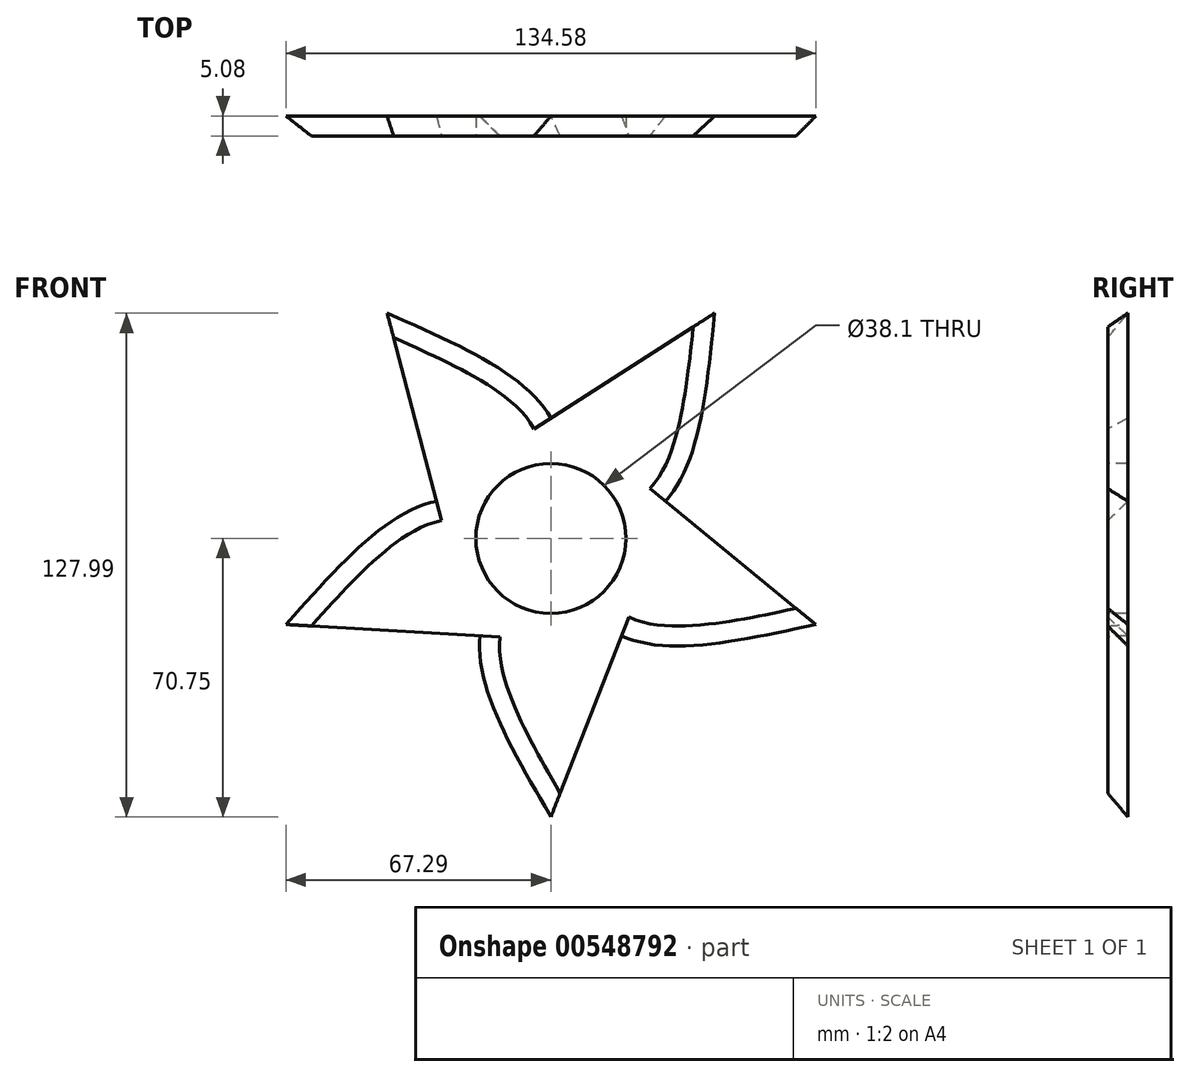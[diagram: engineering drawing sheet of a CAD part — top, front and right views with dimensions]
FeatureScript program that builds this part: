
annotation { "Feature Type Name" : "Feature", "Feature Type Description" : "" }
export const myFeature = defineFeature(function(context is Context, id is Id, definition is map)
    precondition{}
    {
        {
            var Q0;
            Q0=qCreatedBy(makeId("Front.planeOp"),FACE);
            var sketch = newSketch(context, id + "F0", { "sketchPlane" : qUnion([Q0])});
            skLineSegment(sketch, "E0.0", {"start": v(-41.59, 57.24) * mm, "end": v(41.59, 57.24) * mm});
            skLineSegment(sketch, "E0.1", {"start": v(41.59, 57.24) * mm, "end": v(67.3, -21.86) * mm});
            skLineSegment(sketch, "E0.2", {"start": v(67.3, -21.86) * mm, "end": v(0, -70.75) * mm});
            skLineSegment(sketch, "E0.3", {"start": v(0, -70.75) * mm, "end": v(-67.3, -21.86) * mm});
            skLineSegment(sketch, "E0.4", {"start": v(-67.3, -21.86) * mm, "end": v(-41.59, 57.24) * mm});
            skPoint(sketch, "E0.0.midPoint", {"position": v(0, 57.24) * mm});
            skLineSegment(sketch, "E1", {"start": v(-67.3, -21.86) * mm, "end": v(0, 0) * mm});
            skLineSegment(sketch, "E2", {"start": v(-41.59, 57.24) * mm, "end": v(0, 0) * mm});
            skLineSegment(sketch, "E3", {"start": v(41.59, 57.24) * mm, "end": v(0, 0) * mm});
            skLineSegment(sketch, "E4", {"start": v(0, -70.75) * mm, "end": v(0, 0) * mm});
            skLineSegment(sketch, "E5", {"start": v(67.3, -21.86) * mm, "end": v(0, 0) * mm});
            skPoint(sketch, "E6.0.midPoint", {"position": v(0, -24.72) * mm});
            skPoint(sketch, "E7", {"position": v(0, 30.56) * mm});
            skPoint(sketch, "E8", {"position": v(-29.07, 9.44) * mm});
            skPoint(sketch, "E9", {"position": v(-17.96, -24.72) * mm});
            skPoint(sketch, "E10", {"position": v(17.96, -24.72) * mm});
            skPoint(sketch, "E11", {"position": v(29.07, 9.44) * mm});
            skFitSpline(sketch, "E12", {"points": [v(-67.3, -21.86) * mm, v(-29.07, 9.44) * mm, v(0, 0) * mm], "startDerivative": vector(68.92, 77.59) * mm, "endDerivative": vector(65.52, -38.49) * mm});
            skFitSpline(sketch, "E13", {"points": [v(-41.59, 57.24) * mm, v(0, 30.56) * mm, v(0, 0) * mm], "startDerivative": vector(95.09, -41.57) * mm, "endDerivative": vector(-16.35, -74.2) * mm});
            skFitSpline(sketch, "E14", {"points": [v(41.59, 57.24) * mm, v(29.07, 9.44) * mm, v(0, 0) * mm], "startDerivative": vector(-10.15, -103.28) * mm, "endDerivative": vector(-75.63, -7.38) * mm});
            skFitSpline(sketch, "E15", {"points": [v(67.3, -21.86) * mm, v(17.96, -24.72) * mm, v(0, 0) * mm], "startDerivative": vector(-101.37, -22.26) * mm, "endDerivative": vector(-30.39, 69.65) * mm});
            skFitSpline(sketch, "E16", {"points": [v(0, -70.75) * mm, v(-17.96, -24.72) * mm, v(0, 0) * mm], "startDerivative": vector(-52.5, 89.53) * mm, "endDerivative": vector(56.85, 50.42) * mm});
            skPoint(sketch, "E17", {"position": v(2.74, 20) * mm});
            skPoint(sketch, "E18", {"position": v(19.87, 3.58) * mm});
            skPoint(sketch, "E19", {"position": v(9.54, -17.8) * mm});
            skPoint(sketch, "E20", {"position": v(-13.97, -14.57) * mm});
            skPoint(sketch, "E21", {"position": v(-18.18, 8.78) * mm});
            skLineSegment(sketch, "E22", {"start": v(9.54, -17.8) * mm, "end": v(0, -70.75) * mm});
            skLineSegment(sketch, "E23", {"start": v(19.87, 3.58) * mm, "end": v(67.3, -21.86) * mm});
            skLineSegment(sketch, "E24", {"start": v(-13.97, -14.57) * mm, "end": v(-67.3, -21.86) * mm});
            skLineSegment(sketch, "E25", {"start": v(-29.07, 9.44) * mm, "end": v(-41.59, 57.24) * mm});
            skLineSegment(sketch, "E26", {"start": v(0, 30.56) * mm, "end": v(41.59, 57.24) * mm});
            skLineSegment(sketch, "E27", {"start": v(29.07, 9.44) * mm, "end": v(67.3, -21.86) * mm});
            skLineSegment(sketch, "E28", {"start": v(17.96, -24.72) * mm, "end": v(0, -70.75) * mm});
            skLineSegment(sketch, "E29", {"start": v(-67.3, -21.86) * mm, "end": v(-17.96, -24.72) * mm});
            skLineSegment(sketch, "E30", {"start": v(-41.59, 57.24) * mm, "end": v(-18.18, 8.78) * mm});
            skLineSegment(sketch, "E31", {"start": v(2.74, 20) * mm, "end": v(41.59, 57.24) * mm});
            skLineSegment(sketch, "E32", {"start": v(-41.59, 57.24) * mm, "end": v(-34.1, 41.72) * mm});
            skLineSegment(sketch, "E33", {"start": v(-34.1, 41.72) * mm, "end": v(-22.08, 16.87) * mm});
            skLineSegment(sketch, "E34", {"start": v(9.23, 26.22) * mm, "end": v(29.16, 45.32) * mm});
            skLineSegment(sketch, "E35", {"start": v(27.8, -0.67) * mm, "end": v(52.12, -13.72) * mm});
            skLineSegment(sketch, "E36", {"start": v(3.05, -53.8) * mm, "end": v(7.95, -26.64) * mm});
            skLineSegment(sketch, "E37", {"start": v(-50.23, -19.53) * mm, "end": v(-22.88, -15.8) * mm});
            skSolve(sketch);
        }
        {
            var Q0;
            {var subQ0=sQuery(id+"F0.wireOp",EDGE,"E1");Q0=makeQuery(id+"F0.imprint","IMPRINT",FACE,{"disambiguationData":[TD([[makeQuery(id+"F0.imprint","IMPRINT",EDGE,{"derivedFrom":subQ0}),-1.0]])]});}
            var Q1;
            {var subQ0=sQuery(id+"F0.wireOp",EDGE,"E2");Q1=makeQuery(id+"F0.imprint","IMPRINT",FACE,{"disambiguationData":[TD([[makeQuery(id+"F0.imprint","IMPRINT",EDGE,{"derivedFrom":subQ0}),-1.0]])]});}
            var Q2;
            {var subQ0=sQuery(id+"F0.wireOp",EDGE,"E3");Q2=makeQuery(id+"F0.imprint","IMPRINT",FACE,{"disambiguationData":[TD([[makeQuery(id+"F0.imprint","IMPRINT",EDGE,{"derivedFrom":subQ0}),-1.0]])]});}
            var Q3;
            {var subQ0=sQuery(id+"F0.wireOp",EDGE,"E4");Q3=makeQuery(id+"F0.imprint","IMPRINT",FACE,{"disambiguationData":[TD([[makeQuery(id+"F0.imprint","IMPRINT",EDGE,{"derivedFrom":subQ0}),-1.0]])]});}
            var Q4;
            {var subQ0=sQuery(id+"F0.wireOp",EDGE,"E5");Q4=makeQuery(id+"F0.imprint","IMPRINT",FACE,{"disambiguationData":[TD([[makeQuery(id+"F0.imprint","IMPRINT",EDGE,{"derivedFrom":subQ0}),-1.0]])]});}
            var Q5;
            {var subQ0=sQuery(id+"F0.wireOp",EDGE,"E25");Q5=makeQuery(id+"F0.imprint","IMPRINT",FACE,{"disambiguationData":[TD([[makeQuery(id+"F0.imprint","IMPRINT",EDGE,{"derivedFrom":subQ0}),-1.0]])]});}
            var Q6;
            {var subQ0=sQuery(id+"F0.wireOp",EDGE,"E26");Q6=makeQuery(id+"F0.imprint","IMPRINT",FACE,{"disambiguationData":[TD([[makeQuery(id+"F0.imprint","IMPRINT",EDGE,{"derivedFrom":subQ0}),-1.0]])]});}
            var Q7;
            {var subQ0=sQuery(id+"F0.wireOp",EDGE,"E23");Q7=makeQuery(id+"F0.imprint","IMPRINT",FACE,{"disambiguationData":[TD([[makeQuery(id+"F0.imprint","IMPRINT",EDGE,{"derivedFrom":subQ0}),1.0]])]});}
            var Q8;
            {var subQ0=sQuery(id+"F0.wireOp",EDGE,"E22");Q8=makeQuery(id+"F0.imprint","IMPRINT",FACE,{"disambiguationData":[TD([[makeQuery(id+"F0.imprint","IMPRINT",EDGE,{"derivedFrom":subQ0}),1.0]])]});}
            var Q9;
            {var subQ0=sQuery(id+"F0.wireOp",EDGE,"E24");Q9=makeQuery(id+"F0.imprint","IMPRINT",FACE,{"disambiguationData":[TD([[makeQuery(id+"F0.imprint","IMPRINT",EDGE,{"derivedFrom":subQ0}),1.0]])]});}
            var Q10;
            {var subQ0=sQuery(id+"F0.wireOp",EDGE,"E1");Q10=makeQuery(id+"F0.imprint","IMPRINT",FACE,{"disambiguationData":[TD([[makeQuery(id+"F0.imprint","IMPRINT",EDGE,{"derivedFrom":subQ0}),1.0]])]});}
            var Q11;
            {var subQ0=sQuery(id+"F0.wireOp",EDGE,"E2");Q11=makeQuery(id+"F0.imprint","IMPRINT",FACE,{"disambiguationData":[TD([[makeQuery(id+"F0.imprint","IMPRINT",EDGE,{"derivedFrom":subQ0}),1.0]])]});}
            var Q12;
            {var subQ0=sQuery(id+"F0.wireOp",EDGE,"E3");Q12=makeQuery(id+"F0.imprint","IMPRINT",FACE,{"disambiguationData":[TD([[makeQuery(id+"F0.imprint","IMPRINT",EDGE,{"derivedFrom":subQ0}),1.0]])]});}
            var Q13;
            {var subQ0=sQuery(id+"F0.wireOp",EDGE,"E4");Q13=makeQuery(id+"F0.imprint","IMPRINT",FACE,{"disambiguationData":[TD([[makeQuery(id+"F0.imprint","IMPRINT",EDGE,{"derivedFrom":subQ0}),1.0]])]});}
            var Q14;
            {var subQ0=sQuery(id+"F0.wireOp",EDGE,"E5");Q14=makeQuery(id+"F0.imprint","IMPRINT",FACE,{"disambiguationData":[TD([[makeQuery(id+"F0.imprint","IMPRINT",EDGE,{"derivedFrom":subQ0}),1.0]])]});}
            extrude(context, id + "F1", {"entities" : qUnion([Q0, Q1, Q2, Q3, Q4, Q5, Q6, Q7, Q8, Q9, Q10, Q11, Q12, Q13, Q14]), "endBound" : BoundingType.SYMMETRIC, "depth" : 5.08 * mm, "offsetDistance" : 25.4 * mm});
        }
        {
            var Q0;
            Q0=makeQuery(id+"F1.opExtrude","CAP_EDGE",EDGE,{"disambiguationData":[OSD([sQuery(id+"F0.wireOp",EDGE,"E16")])],"isStart":false});
            var Q1;
            Q1=makeQuery(id+"F1.opExtrude","CAP_EDGE",EDGE,{"disambiguationData":[OSD([sQuery(id+"F0.wireOp",EDGE,"E15")])],"isStart":false});
            var Q2;
            Q2=makeQuery(id+"F1.opExtrude","CAP_EDGE",EDGE,{"disambiguationData":[OSD([sQuery(id+"F0.wireOp",EDGE,"E14")])],"isStart":false});
            var Q3;
            Q3=makeQuery(id+"F1.opExtrude","CAP_EDGE",EDGE,{"disambiguationData":[OSD([sQuery(id+"F0.wireOp",EDGE,"E13")])],"isStart":false});
            var Q4;
            Q4=makeQuery(id+"F1.opExtrude","CAP_EDGE",EDGE,{"disambiguationData":[OSD([sQuery(id+"F0.wireOp",EDGE,"E12")])],"isStart":false});
            chamfer(context, id + "F2", {"entities" : qUnion([Q0, Q1, Q2, Q3, Q4]), "width" : 5.08 * mm, "tangentPropagation" : true});
        }
        {
            var Q0;
            Q0=makeQuery(id+"F1.opExtrude","CAP_FACE",FACE,{"disambiguationData":[OSD([sQuery(id+"F0.wireOp",EDGE,"E12"),sQuery(id+"F0.wireOp",EDGE,"E13"),sQuery(id+"F0.wireOp",EDGE,"E14"),sQuery(id+"F0.wireOp",EDGE,"E15"),sQuery(id+"F0.wireOp",EDGE,"E16"),sQuery(id+"F0.wireOp",EDGE,"E25"),sQuery(id+"F0.wireOp",EDGE,"E26"),sQuery(id+"F0.wireOp",EDGE,"E27"),sQuery(id+"F0.wireOp",EDGE,"E28"),sQuery(id+"F0.wireOp",EDGE,"E29")])],"isStart":false});
            var sketch = newSketch(context, id + "F3", { "sketchPlane" : qUnion([Q0])});
            skCircle(sketch, "E38", {"center": v(0, 0) * mm, "radius": 19.05 * mm});
            skPoint(sketch, "E39", {"position": v(-34.06, 41.66) * mm});
            skPoint(sketch, "E40", {"position": v(-22.02, 16.8) * mm});
            skPoint(sketch, "E41", {"position": v(9.28, 26.24) * mm});
            skPoint(sketch, "E42", {"position": v(29.14, 45.28) * mm});
            skPoint(sketch, "E43", {"position": v(27.86, -0.77) * mm});
            skPoint(sketch, "E44", {"position": v(52.09, -13.78) * mm});
            skPoint(sketch, "E45", {"position": v(7.96, -26.69) * mm});
            skPoint(sketch, "E46", {"position": v(3.1, -53.8) * mm});
            skPoint(sketch, "E47", {"position": v(-22.85, -15.81) * mm});
            skPoint(sketch, "E48", {"position": v(-50.2, -19.54) * mm});
            skCircle(sketch, "E49", {"center": v(0, 0) * mm, "radius": 27.83 * mm});
            skPoint(sketch, "E50", {"position": v(-10.99, 25.57) * mm});
            skPoint(sketch, "E51", {"position": v(-4.29, 27.8) * mm});
            skPoint(sketch, "E52", {"position": v(25.12, 12.67) * mm});
            skPoint(sketch, "E53", {"position": v(20.9, 18.38) * mm});
            skPoint(sketch, "E54", {"position": v(19.82, -19.98) * mm});
            skPoint(sketch, "E55", {"position": v(23.93, -14.2) * mm});
            skPoint(sketch, "E56", {"position": v(-12.88, -25.02) * mm});
            skPoint(sketch, "E57", {"position": v(-6.13, -27.15) * mm});
            skPoint(sketch, "E58", {"position": v(-27.77, 4.51) * mm});
            skPoint(sketch, "E59", {"position": v(-27.71, -2.6) * mm});
            skSolve(sketch);
        }
        {
            var Q0;
            Q0=makeQuery(id+"F3.imprint","IMPRINT",FACE,{"disambiguationData":[TD([[makeQuery(id+"F3.imprint","IMPRINT",EDGE,{"derivedFrom":sQuery(id+"F3.wireOp",EDGE,"E38")}),1.0]])]});
            extrude(context, id + "F4", {"entities" : qUnion([Q0]), "operationType" : NewBodyOperationType.REMOVE, "endBound" : BoundingType.THROUGH_ALL, "oppositeDirection" : true, "depth" : 25.4 * mm, "offsetDistance" : 25.4 * mm});
        }
    });
